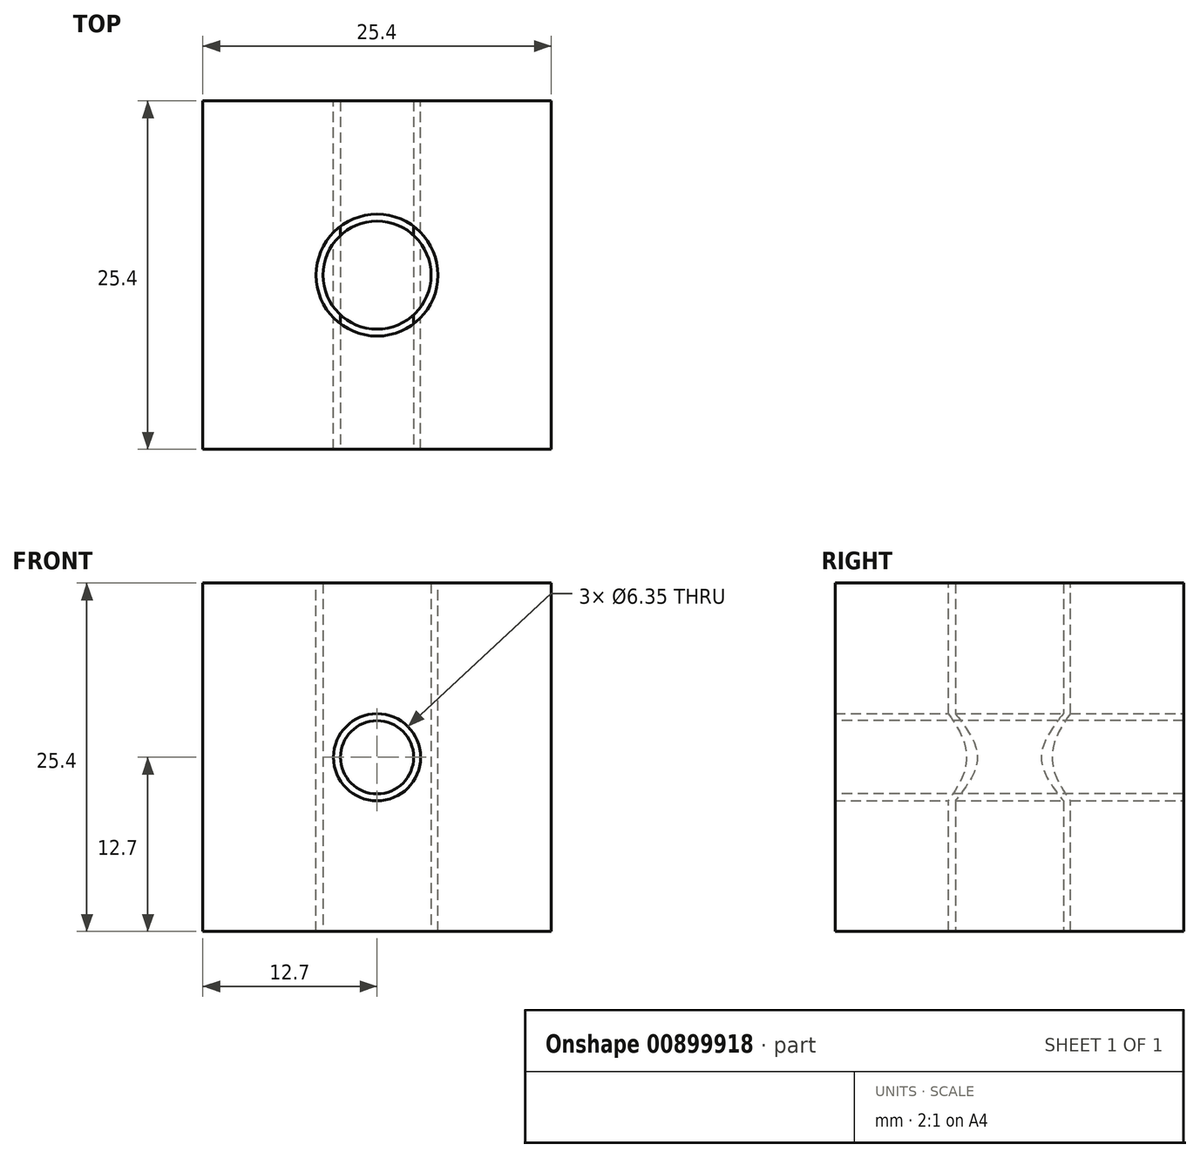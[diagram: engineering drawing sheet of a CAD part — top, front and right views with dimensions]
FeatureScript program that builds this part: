
annotation { "Feature Type Name" : "Feature", "Feature Type Description" : "" }
export const myFeature = defineFeature(function(context is Context, id is Id, definition is map)
    precondition{}
    {
        {
            var Q0;
            Q0=qCreatedBy(makeId("Top.planeOp"),FACE);
            var sketch = newSketch(context, id + "F0", { "sketchPlane" : qUnion([Q0])});
            skLineSegment(sketch, "E0.bottom", {"start": v(12.7, -12.7) * mm, "end": v(-12.7, -12.7) * mm});
            skLineSegment(sketch, "E0.top", {"start": v(12.7, 12.7) * mm, "end": v(-12.7, 12.7) * mm});
            skLineSegment(sketch, "E0.left", {"start": v(12.7, -12.7) * mm, "end": v(12.7, 12.7) * mm});
            skLineSegment(sketch, "E0.right", {"start": v(-12.7, -12.7) * mm, "end": v(-12.7, 12.7) * mm});
            skPoint(sketch, "E0.middle", {"position": v(0, 0) * mm});
            skSolve(sketch);
        }
        {
            var Q0;
            Q0 = qSketchRegion(id + "F0", true);
            extrude(context, id + "F1", {"entities" : qUnion([Q0]), "depth" : 25.4 * mm, "offsetDistance" : 25.4 * mm});
        }
        {
            var Q0;
            Q0=makeQuery(id+"F1.opExtrude","CAP_FACE",FACE,{"disambiguationData":[OSD([sQuery(id+"F0.wireOp",EDGE,"E0.bottom"),sQuery(id+"F0.wireOp",EDGE,"E0.top"),sQuery(id+"F0.wireOp",EDGE,"E0.left"),sQuery(id+"F0.wireOp",EDGE,"E0.right")])],"isStart":false});
            var sketch = newSketch(context, id + "F2", { "sketchPlane" : qUnion([Q0])});
            skCircle(sketch, "E1", {"center": v(0, 0) * mm, "radius": 4.45 * mm});
            skSolve(sketch);
        }
        {
            var Q0;
            Q0 = qSketchRegion(id + "F2", true);
            extrude(context, id + "F3", {"entities" : qUnion([Q0]), "operationType" : NewBodyOperationType.REMOVE, "endBound" : BoundingType.THROUGH_ALL, "oppositeDirection" : true, "depth" : 25.4 * mm, "offsetDistance" : 25.4 * mm});
        }
        {
            var Q0;
            Q0=makeQuery(id+"F1.opExtrude","SWEPT_FACE",FACE,{"disambiguationData":[OSD([sQuery(id+"F0.wireOp",EDGE,"E0.top")])]});
            var sketch = newSketch(context, id + "F4", { "sketchPlane" : qUnion([Q0])});
            skLineSegment(sketch, "E2", {"start": v(0, 0) * mm, "end": v(0, 25.4) * mm, "construction": true});
            skCircle(sketch, "E3", {"center": v(0, 12.7) * mm, "radius": 3.18 * mm});
            skSolve(sketch);
        }
        {
            var Q0;
            Q0=makeQuery(id+"F1.opExtrude","CAP_FACE",FACE,{"disambiguationData":[OSD([sQuery(id+"F0.wireOp",EDGE,"E0.bottom"),sQuery(id+"F0.wireOp",EDGE,"E0.top"),sQuery(id+"F0.wireOp",EDGE,"E0.left"),sQuery(id+"F0.wireOp",EDGE,"E0.right")])],"isStart":true});
            var sketch = newSketch(context, id + "F5", { "sketchPlane" : qUnion([Q0])});
            skCircle(sketch, "E4.0", {"center": v(0, 0) * mm, "radius": 3.94 * mm});
            skSolve(sketch);
        }
        {
            var Q0;
            Q0 = qSketchRegion(id + "F5", true);
            var Q1;
            Q1=makeQuery(id+"F1.opExtrude","CAP_FACE",FACE,{"disambiguationData":[OSD([sQuery(id+"F0.wireOp",EDGE,"E0.bottom"),sQuery(id+"F0.wireOp",EDGE,"E0.top"),sQuery(id+"F0.wireOp",EDGE,"E0.left"),sQuery(id+"F0.wireOp",EDGE,"E0.right")])],"isStart":false});
            extrude(context, id + "F6", {"entities" : qUnion([Q0]), "endBound" : BoundingType.UP_TO_SURFACE, "oppositeDirection" : true, "depth" : 25.4 * mm, "endBoundEntityFace" : qUnion([Q1]), "offsetDistance" : 25.4 * mm});
        }
        {
            var Q0;
            Q0 = qSketchRegion(id + "F4", true);
            extrude(context, id + "F7", {"entities" : qUnion([Q0]), "operationType" : NewBodyOperationType.REMOVE, "endBound" : BoundingType.THROUGH_ALL, "oppositeDirection" : true, "depth" : 25.4 * mm, "offsetDistance" : 25.4 * mm});
        }
        {
            var Q0;
            Q0=makeQuery(id+"F1.opExtrude","SWEPT_FACE",FACE,{"disambiguationData":[OSD([sQuery(id+"F0.wireOp",EDGE,"E0.bottom")])]});
            var sketch = newSketch(context, id + "F8", { "sketchPlane" : qUnion([Q0])});
            skCircle(sketch, "E5.0", {"center": v(0, 12.7) * mm, "radius": 2.67 * mm});
            skSolve(sketch);
        }
        {
            var Q0;
            Q0 = qSketchRegion(id + "F8", true);
            var Q1;
            Q1=makeQuery(id+"F1.opExtrude","SWEPT_FACE",FACE,{"disambiguationData":[OSD([sQuery(id+"F0.wireOp",EDGE,"E0.top")])]});
            extrude(context, id + "F9", {"entities" : qUnion([Q0]), "endBound" : BoundingType.UP_TO_SURFACE, "oppositeDirection" : true, "depth" : 25.4 * mm, "endBoundEntityFace" : qUnion([Q1]), "offsetDistance" : 25.4 * mm});
        }
    });
